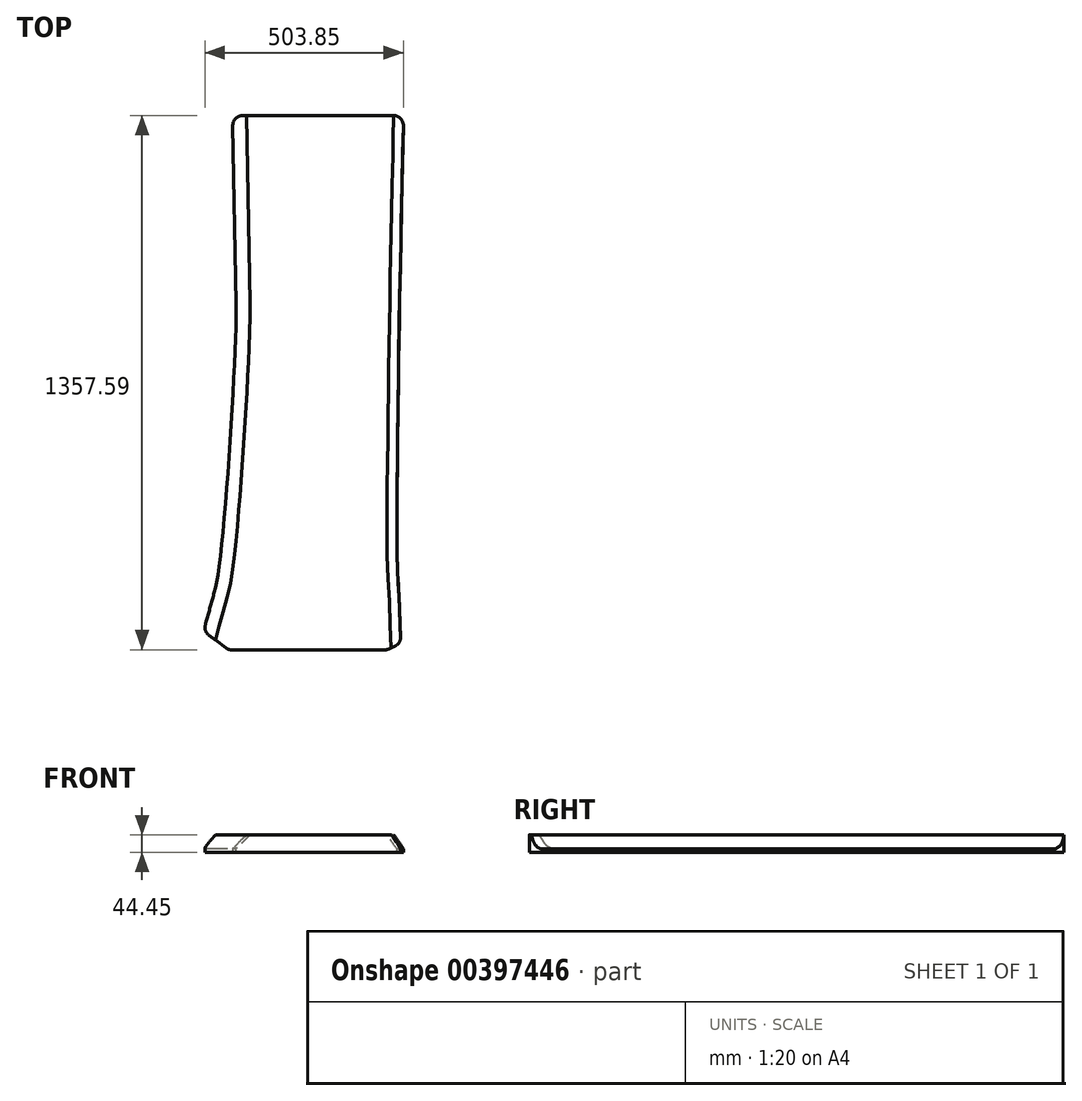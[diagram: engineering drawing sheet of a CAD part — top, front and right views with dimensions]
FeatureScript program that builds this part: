
annotation { "Feature Type Name" : "Feature", "Feature Type Description" : "" }
export const myFeature = defineFeature(function(context is Context, id is Id, definition is map)
    precondition{}
    {
        {
            var Q0;
            Q0=qCreatedBy(makeId("Top.planeOp"),FACE);
            var sketch = newSketch(context, id + "F0", { "sketchPlane" : qUnion([Q0])});
            skLineSegment(sketch, "E0", {"start": v(254, 685.8) * mm, "end": v(-254, -685.8) * mm, "construction": true});
            skLineSegment(sketch, "E1", {"start": v(254, 685.8) * mm, "end": v(-180.32, 685.8) * mm});
            skLineSegment(sketch, "E2", {"start": v(-180.32, 685.8) * mm, "end": v(-170.95, 208.11) * mm});
            skLineSegment(sketch, "E3", {"start": v(212.08, -671.8) * mm, "end": v(-190.7, -671.8) * mm});
            skLineSegment(sketch, "E4", {"start": v(-190.7, -671.8) * mm, "end": v(-254, -624.68) * mm});
            skLineSegment(sketch, "E5", {"start": v(-254, -624.68) * mm, "end": v(-223.6, -513.5) * mm});
            skFitSpline(sketch, "E6", {"points": [v(-170.95, 208.11) * mm, v(-223.6, -513.5) * mm], "startDerivative": vector(6.23, -317.63) * mm, "endDerivative": vector(-68.87, -251.84) * mm});
            skLineSegment(sketch, "E7", {"start": v(212.08, -671.8) * mm, "end": v(247.23, -655.35) * mm});
            skFitSpline(sketch, "E8", {"points": [v(247.23, -655.35) * mm, v(243.17, -552.5) * mm, v(237.78, -437.62) * mm, v(237.78, -242.64) * mm, v(243.8, 194.02) * mm, v(254, 685.8) * mm], "startDerivative": vector(-36.31, 626.23) * mm, "endDerivative": vector(36.12, 1726.78) * mm});
            skSolve(sketch);
        }
        {
            var Q0;
            Q0 = qSketchRegion(id + "F0", true);
            extrude(context, id + "F1", {"entities" : qUnion([Q0]), "depth" : 44.45 * mm});
        }
        {
            var Q0;
            Q0=makeQuery(id+"F1.opExtrude","SWEPT_EDGE",EDGE,{"disambiguationData":[OSD([sQuery(id+"F0.wireOp",EDGE,"gtoLgGXa-ZG0s-d6Xa-uOR6-zl5Qnj0gpUux"),sQuery(id+"F0.wireOp",EDGE,"os8Rb0C4-p9va-katC-NM4Q-daP3BzwpEXIg")])]});
            var Q1;
            Q1=makeQuery(id+"F1.opExtrude","SWEPT_EDGE",EDGE,{"disambiguationData":[OSD([sQuery(id+"F0.wireOp",EDGE,"ujFNgLCE-HfiO-Vezh-0N4z-Y0Mxlg9P2K10"),sQuery(id+"F0.wireOp",EDGE,"gtoLgGXa-ZG0s-d6Xa-uOR6-zl5Qnj0gpUux")])]});
            var Q2;
            Q2=makeQuery(id+"F1.opExtrude","SWEPT_EDGE",EDGE,{"disambiguationData":[OSD([sQuery(id+"F0.wireOp",EDGE,"RqLCQjLu-10nL-UyCL-hCps-LsxCMnfALXwT"),sQuery(id+"F0.wireOp",EDGE,"ujFNgLCE-HfiO-Vezh-0N4z-Y0Mxlg9P2K10")])]});
            var Q3;
            Q3=makeQuery(id+"F1.opExtrude","SWEPT_EDGE",EDGE,{"disambiguationData":[OSD([sQuery(id+"F0.wireOp",EDGE,"58KnjvqM-R6Rl-kx9d-b5Ux-AN5yOqaP6P0r"),sQuery(id+"F0.wireOp",EDGE,"RqLCQjLu-10nL-UyCL-hCps-LsxCMnfALXwT")])]});
            var Q4;
            Q4=makeQuery(id+"F1.opExtrude","SWEPT_EDGE",EDGE,{"disambiguationData":[OSD([sQuery(id+"F0.wireOp",EDGE,"58KnjvqM-R6Rl-kx9d-b5Ux-AN5yOqaP6P0r"),sQuery(id+"F0.wireOp",EDGE,"FL5bADye-6Ln2-j86k-TWtk-85oBJg9EQknC")])]});
            var Q5;
            Q5=makeQuery(id+"F1.opExtrude","SWEPT_EDGE",EDGE,{"disambiguationData":[OSD([sQuery(id+"F0.wireOp",EDGE,"bsTn7xqM-EpRR-0M3m-Grpk-YTB3m2WXlTfn"),sQuery(id+"F0.wireOp",EDGE,"FL5bADye-6Ln2-j86k-TWtk-85oBJg9EQknC")])]});
            var Q6;
            Q6=makeQuery(id+"F1.opExtrude","SWEPT_EDGE",EDGE,{"disambiguationData":[OSD([sQuery(id+"F0.wireOp",EDGE,"kcCxaifr-XVqK-Jllh-MBXd-2CT7PWzywqcI"),sQuery(id+"F0.wireOp",EDGE,"bsTn7xqM-EpRR-0M3m-Grpk-YTB3m2WXlTfn")])]});
            var Q7;
            Q7=makeQuery(id+"F1.opExtrude","SWEPT_EDGE",EDGE,{"disambiguationData":[OSD([sQuery(id+"F0.wireOp",EDGE,"mL9R2Iii-wL04-kh4f-yr7n-L4uOFpdJl0xV"),sQuery(id+"F0.wireOp",EDGE,"kcCxaifr-XVqK-Jllh-MBXd-2CT7PWzywqcI")])]});
            var Q8;
            Q8=makeQuery(id+"F1.opExtrude","SWEPT_EDGE",EDGE,{"disambiguationData":[OSD([sQuery(id+"F0.wireOp",EDGE,"8UidgXFO-N6Iq-QVcI-ioFO-zdAMqTSYye7i"),sQuery(id+"F0.wireOp",EDGE,"mL9R2Iii-wL04-kh4f-yr7n-L4uOFpdJl0xV")])]});
            var Q9;
            Q9=makeQuery(id+"F1.opExtrude","SWEPT_EDGE",EDGE,{"disambiguationData":[OSD([sQuery(id+"F0.wireOp",EDGE,"os8Rb0C4-p9va-katC-NM4Q-daP3BzwpEXIg"),sQuery(id+"F0.wireOp",EDGE,"bP6kMfsC-DnyU-awwU-iuG1-yvlgNmt88Zod")])]});
            var Q10;
            Q10=makeQuery(id+"F1.opExtrude","SWEPT_EDGE",EDGE,{"disambiguationData":[OSD([sQuery(id+"F0.wireOp",EDGE,"bP6kMfsC-DnyU-awwU-iuG1-yvlgNmt88Zod"),sQuery(id+"F0.wireOp",EDGE,"8UidgXFO-N6Iq-QVcI-ioFO-zdAMqTSYye7i")])]});
            var Q11;
            Q11=makeQuery(id+"F1.opExtrude","SWEPT_EDGE",EDGE,{"disambiguationData":[OSD([sQuery(id+"F0.wireOp",EDGE,"E3"),sQuery(id+"F0.wireOp",EDGE,"E7")])]});
            var Q12;
            Q12=makeQuery(id+"F1.opExtrude","SWEPT_EDGE",EDGE,{"disambiguationData":[OSD([sQuery(id+"F0.wireOp",EDGE,"E7"),sQuery(id+"F0.wireOp",EDGE,"IDIg36tL-tvEn-4JRp-EukI-vWCSV4OWNaz8")])]});
            var Q13;
            Q13=makeQuery(id+"F1.opExtrude","SWEPT_EDGE",EDGE,{"disambiguationData":[OSD([sQuery(id+"F0.wireOp",EDGE,"E4"),sQuery(id+"F0.wireOp",EDGE,"E5")])]});
            var Q14;
            Q14=makeQuery(id+"F1.opExtrude","SWEPT_EDGE",EDGE,{"disambiguationData":[OSD([sQuery(id+"F0.wireOp",EDGE,"E3"),sQuery(id+"F0.wireOp",EDGE,"E4")])]});
            var Q15;
            Q15=makeQuery(id+"F1.opExtrude","SWEPT_EDGE",EDGE,{"disambiguationData":[OSD([sQuery(id+"F0.wireOp",EDGE,"E5"),sQuery(id+"F0.wireOp",EDGE,"E6")])]});
            var Q16;
            Q16=makeQuery(id+"F1.opExtrude","SWEPT_EDGE",EDGE,{"disambiguationData":[OSD([sQuery(id+"F0.wireOp",EDGE,"E1"),sQuery(id+"F0.wireOp",EDGE,"E2")])]});
            var Q17;
            Q17=makeQuery(id+"F1.opExtrude","SWEPT_EDGE",EDGE,{"disambiguationData":[OSD([sQuery(id+"F0.wireOp",EDGE,"E1"),sQuery(id+"F0.wireOp",EDGE,"IDIg36tL-tvEn-4JRp-EukI-vWCSV4OWNaz8")])]});
            fillet(context, id + "F2", {"entities" : qUnion([Q0, Q1, Q2, Q3, Q4, Q5, Q6, Q7, Q8, Q9, Q10, Q11, Q12, Q13, Q14, Q15, Q16, Q17]), "radius" : 25 * mm, "tangentPropagation" : true, "allowEdgeOverflow" : false});
        }
        {
            var Q0;
            Q0=makeQuery(id+"F1.opExtrude","CAP_EDGE",EDGE,{"disambiguationData":[OSD([sQuery(id+"F0.wireOp",EDGE,"IDIg36tL-tvEn-4JRp-EukI-vWCSV4OWNaz8")])],"isStart":false});
            var Q1;
            Q1=makeQuery(id+"F1.opExtrude","CAP_EDGE",EDGE,{"disambiguationData":[OSD([sQuery(id+"F0.wireOp",EDGE,"E2")])],"isStart":false});
            var Q2;
            Q2=makeQuery(id+"F1.opExtrude","CAP_EDGE",EDGE,{"disambiguationData":[OSD([sQuery(id+"F0.wireOp",EDGE,"E6")])],"isStart":false});
            chamfer(context, id + "F3", {"entities" : qUnion([Q0, Q1, Q2]), "width" : 35 * mm});
        }
        {
            var Q0;
            Q0=makeQuery(id+"F1.opExtrude","CAP_EDGE",EDGE,{"disambiguationData":[OSD([sQuery(id+"F0.wireOp",EDGE,"E8")])],"isStart":false});
            chamfer(context, id + "F4", {"entities" : qUnion([Q0]), "chamferType" : ChamferType.OFFSET_ANGLE, "width" : 25 * mm, "oppositeDirection" : false, "angle" : 55 * degree});
        }
        {
            var Q0;
            Q0=makeQuery(id+"F1.opExtrude","CAP_FACE",FACE,{"disambiguationData":[OSD([sQuery(id+"F0.wireOp",EDGE,"E1"),sQuery(id+"F0.wireOp",EDGE,"E2"),sQuery(id+"F0.wireOp",EDGE,"E3"),sQuery(id+"F0.wireOp",EDGE,"E4"),sQuery(id+"F0.wireOp",EDGE,"E5"),sQuery(id+"F0.wireOp",EDGE,"E6"),sQuery(id+"F0.wireOp",EDGE,"E7"),sQuery(id+"F0.wireOp",EDGE,"IDIg36tL-tvEn-4JRp-EukI-vWCSV4OWNaz8")])],"isStart":true});
            var sketch = newSketch(context, id + "F5", { "sketchPlane" : qUnion([Q0])});
            skLineSegment(sketch, "E9", {"start": v(16.54, 671.8) * mm, "end": v(16.54, 570.2) * mm, "construction": true});
            skLineSegment(sketch, "E10", {"start": v(16.54, 570.2) * mm, "end": v(16.54, -584.2) * mm, "construction": true});
            skLineSegment(sketch, "E11", {"start": v(16.54, -584.2) * mm, "end": v(16.54, -685.8) * mm, "construction": true});
            skPoint(sketch, "E12", {"position": v(16.54, 570.2) * mm});
            skPoint(sketch, "E13", {"position": v(16.54, -584.2) * mm});
            skSolve(sketch);
        }
    });
